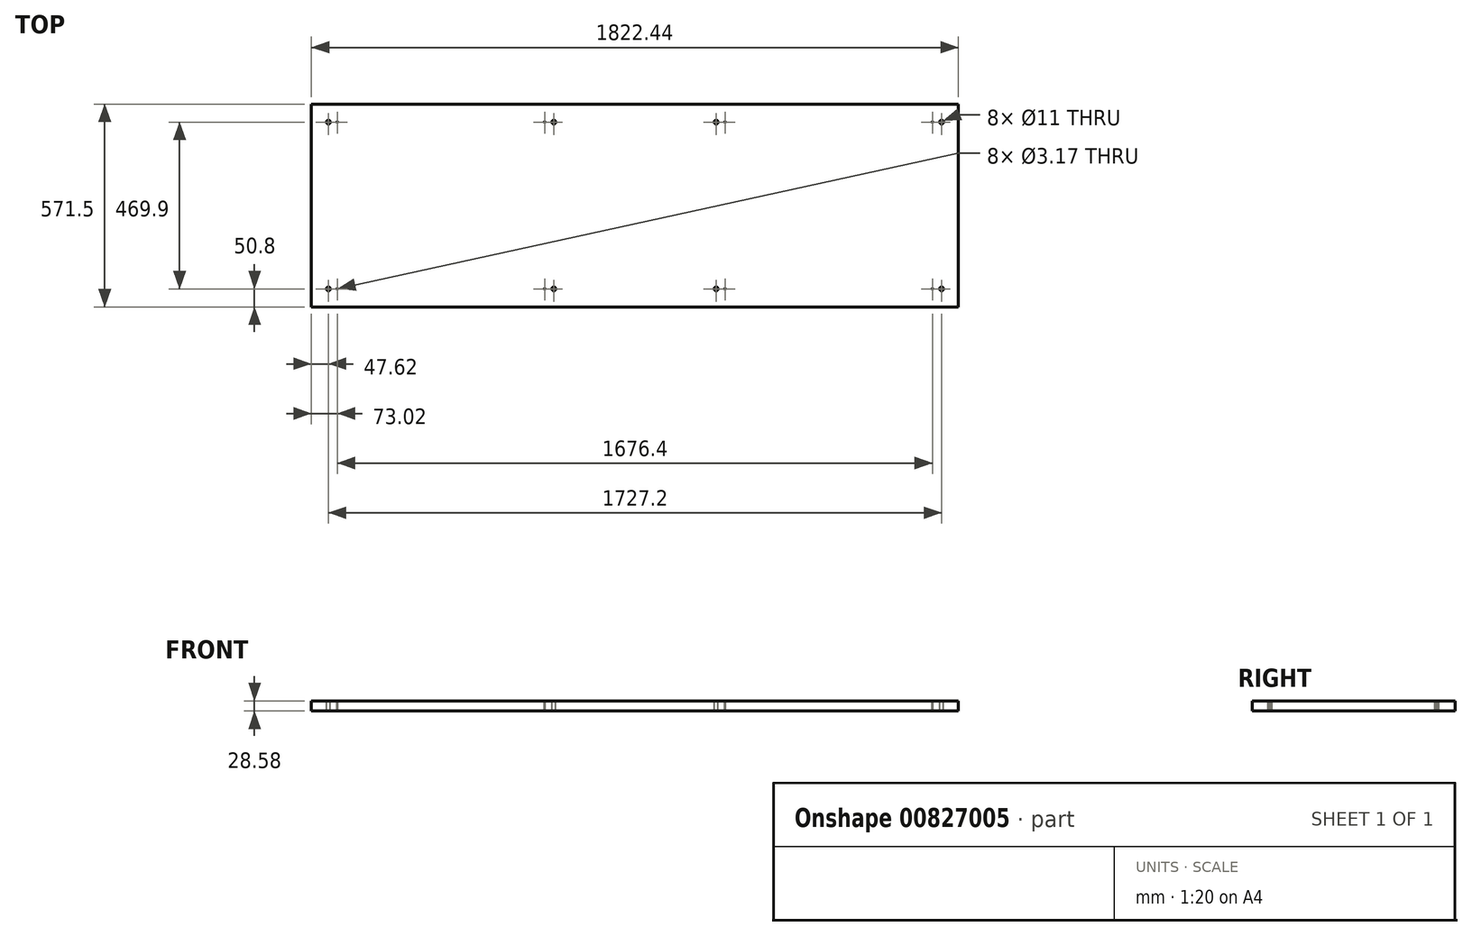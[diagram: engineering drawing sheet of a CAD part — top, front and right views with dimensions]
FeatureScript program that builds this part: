
annotation { "Feature Type Name" : "Feature", "Feature Type Description" : "" }
export const myFeature = defineFeature(function(context is Context, id is Id, definition is map)
    precondition{}
    {
        {
            var Q0;
            Q0=qCreatedBy(makeId("Top.planeOp"),FACE);
            var sketch = newSketch(context, id + "F0", { "sketchPlane" : qUnion([Q0])});
            skLineSegment(sketch, "E0.bottom", {"start": v(911.22, 285.75) * mm, "end": v(-911.22, 285.75) * mm});
            skLineSegment(sketch, "E0.top", {"start": v(911.22, -285.75) * mm, "end": v(-911.22, -285.75) * mm});
            skLineSegment(sketch, "E0.left", {"start": v(911.22, 285.75) * mm, "end": v(911.22, -285.75) * mm});
            skLineSegment(sketch, "E0.right", {"start": v(-911.22, 285.75) * mm, "end": v(-911.22, -285.75) * mm});
            skPoint(sketch, "E0.middle", {"position": v(0, 0) * mm});
            skSolve(sketch);
        }
        {
            var Q0;
            Q0=makeQuery(id+"F0.imprint","IMPRINT",FACE,{"disambiguationData":[TD([[makeQuery(id+"F0.imprint","IMPRINT",EDGE,{"derivedFrom":sQuery(id+"F0.wireOp",EDGE,"E0.bottom")}),1.0]])]});
            extrude(context, id + "F1", {"entities" : qUnion([Q0]), "depth" : 28.57 * mm, "offsetDistance" : 25.4 * mm});
        }
        {
            var Q0;
            Q0=makeQuery(id+"F1.opExtrude","CAP_FACE",FACE,{"disambiguationData":[OSD([sQuery(id+"F0.wireOp",EDGE,"E0.bottom"),sQuery(id+"F0.wireOp",EDGE,"E0.top"),sQuery(id+"F0.wireOp",EDGE,"E0.left"),sQuery(id+"F0.wireOp",EDGE,"E0.right")])],"isStart":false});
            var sketch = newSketch(context, id + "F2", { "sketchPlane" : qUnion([Q0])});
            skLineSegment(sketch, "E1.bottom", {"start": v(863.6, 234.95) * mm, "end": v(-863.6, 234.95) * mm});
            skLineSegment(sketch, "E1.top", {"start": v(863.6, -234.95) * mm, "end": v(-863.6, -234.95) * mm});
            skLineSegment(sketch, "E1.left", {"start": v(863.6, 234.95) * mm, "end": v(863.6, -234.95) * mm});
            skLineSegment(sketch, "E1.right", {"start": v(-863.6, 234.95) * mm, "end": v(-863.6, -234.95) * mm});
            skPoint(sketch, "E1.middle", {"position": v(0, 0) * mm});
            skLineSegment(sketch, "E2.bottom", {"start": v(228.6, 234.95) * mm, "end": v(-228.6, 234.95) * mm});
            skLineSegment(sketch, "E2.top", {"start": v(228.6, -234.95) * mm, "end": v(-228.6, -234.95) * mm});
            skLineSegment(sketch, "E2.left", {"start": v(228.6, 234.95) * mm, "end": v(228.6, -234.95) * mm});
            skLineSegment(sketch, "E2.right", {"start": v(-228.6, 234.95) * mm, "end": v(-228.6, -234.95) * mm});
            skLineSegment(sketch, "E3", {"start": v(-863.6, 234.95) * mm, "end": v(-838.2, 234.95) * mm});
            skLineSegment(sketch, "E4", {"start": v(-228.6, 234.95) * mm, "end": v(-254, 234.95) * mm});
            skLineSegment(sketch, "E5", {"start": v(228.6, 234.95) * mm, "end": v(254, 234.95) * mm});
            skLineSegment(sketch, "E6", {"start": v(863.6, 234.95) * mm, "end": v(838.2, 234.95) * mm});
            skLineSegment(sketch, "E7", {"start": v(-863.6, -234.95) * mm, "end": v(-838.2, -234.95) * mm});
            skLineSegment(sketch, "E8", {"start": v(-228.6, -234.95) * mm, "end": v(-254, -234.95) * mm});
            skLineSegment(sketch, "E9", {"start": v(228.6, -234.95) * mm, "end": v(254, -234.95) * mm});
            skLineSegment(sketch, "E10", {"start": v(863.6, -234.95) * mm, "end": v(838.2, -234.95) * mm});
            skPoint(sketch, "E11", {"position": v(-838.2, 234.95) * mm});
            skPoint(sketch, "E12", {"position": v(-838.2, -234.95) * mm});
            skPoint(sketch, "E13", {"position": v(-254, 234.95) * mm});
            skPoint(sketch, "E14", {"position": v(-254, -234.95) * mm});
            skPoint(sketch, "E15", {"position": v(254, 234.95) * mm});
            skPoint(sketch, "E16", {"position": v(254, -234.95) * mm});
            skPoint(sketch, "E17", {"position": v(838.2, -234.95) * mm});
            skPoint(sketch, "E18", {"position": v(838.2, 234.95) * mm});
            skSolve(sketch);
        }
        {
            var Q0;
            Q0=sQuery(id+"F2.wireOp",VERTEX,"E1.bottom.end");
            var Q1;
            Q1=sQuery(id+"F2.wireOp",VERTEX,"E1.top.end");
            var Q2;
            Q2=sQuery(id+"F2.wireOp",VERTEX,"E2.top.end");
            var Q3;
            Q3=sQuery(id+"F2.wireOp",VERTEX,"E2.bottom.end");
            var Q4;
            Q4=sQuery(id+"F2.wireOp",VERTEX,"E2.bottom.start");
            var Q5;
            Q5=sQuery(id+"F2.wireOp",VERTEX,"E2.top.start");
            var Q6;
            Q6=sQuery(id+"F2.wireOp",VERTEX,"E1.bottom.start");
            var Q7;
            Q7=sQuery(id+"F2.wireOp",VERTEX,"E1.top.start");
            var Q8;
            Q8=makeQuery(id+"F1.opExtrude","SWEPT_BODY",BODY,{"disambiguationData":[OSD([sQuery(id+"F0.wireOp",EDGE,"E0.bottom"),sQuery(id+"F0.wireOp",EDGE,"E0.top"),sQuery(id+"F0.wireOp",EDGE,"E0.left"),sQuery(id+"F0.wireOp",EDGE,"E0.right")])]});
            hole(context, id + "F3", {"style" : HoleStyle.SIMPLE, "endStyle" : HoleEndStyle.BLIND, "holeDiameter" : 11 * mm, "majorDiameter" : 6.35 * mm, "holeDepth" : 31.75 * mm, "isTappedThrough" : true, "tappedDepth" : 12.7 * mm, "tapClearance" : 3, "startFromSketch" : true, "locations" : qUnion([Q0, Q1, Q2, Q3, Q4, Q5, Q6, Q7]), "scope" : qUnion([Q8])});
        }
        {
            var Q0;
            Q0=sQuery(id+"F2.wireOp",VERTEX,"E11");
            var Q1;
            Q1=sQuery(id+"F2.wireOp",VERTEX,"E13");
            var Q2;
            Q2=sQuery(id+"F2.wireOp",VERTEX,"E15");
            var Q3;
            Q3=sQuery(id+"F2.wireOp",VERTEX,"E18");
            var Q4;
            Q4=sQuery(id+"F2.wireOp",VERTEX,"E17");
            var Q5;
            Q5=sQuery(id+"F2.wireOp",VERTEX,"E16");
            var Q6;
            Q6=sQuery(id+"F2.wireOp",VERTEX,"E14");
            var Q7;
            Q7=sQuery(id+"F2.wireOp",VERTEX,"E12");
            var Q8;
            Q8=makeQuery(id+"F1.opExtrude","SWEPT_BODY",BODY,{"disambiguationData":[OSD([sQuery(id+"F0.wireOp",EDGE,"E0.bottom"),sQuery(id+"F0.wireOp",EDGE,"E0.top"),sQuery(id+"F0.wireOp",EDGE,"E0.left"),sQuery(id+"F0.wireOp",EDGE,"E0.right")])]});
            hole(context, id + "F4", {"style" : HoleStyle.SIMPLE, "endStyle" : HoleEndStyle.BLIND, "holeDiameter" : 3.17 * mm, "majorDiameter" : 6.35 * mm, "holeDepth" : 31.75 * mm, "isTappedThrough" : true, "tappedDepth" : 12.7 * mm, "tapClearance" : 3, "startFromSketch" : true, "locations" : qUnion([Q0, Q1, Q2, Q3, Q4, Q5, Q6, Q7]), "scope" : qUnion([Q8])});
        }
    });
